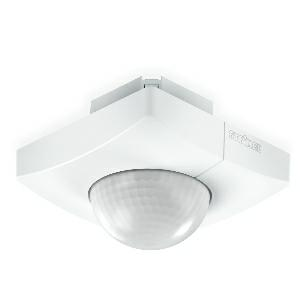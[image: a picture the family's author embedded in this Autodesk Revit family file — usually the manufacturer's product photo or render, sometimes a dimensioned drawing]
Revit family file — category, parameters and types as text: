
# Revit family: is_3360_033491
name_source: partatom
category: Elektroinstallationen
revit_build: Autodesk Revit 2016 (Build: 20190508_0715(x64)
units: mm (PartAtom-declared; Revit-internal decimal feet)

## family parameters
Basisbauteil = Fläche
Beim Laden mit Abzugskörper schneiden = Nein
Bemaßung runder Anschluss = Durchmesser verwenden
Beschriftungsausrichtung beibehalten = Nein
Gemeinsam genutzt = Nein
Raumberechnungspunkt = Nein
Teiletyp = Normal

## types (1)
- IS 3360
    Apparent Load = 0 VA
    Beschreibung = Type: Motion detectors; Dimensions (L x W x H): 78 x 94 x 94 mm; Mains power supply: 220 – 240 V / 50 – 60 Hz; Sensor Technology: passive infrared; Application, place: Indoors; Application, room: production facilities, recreation room, changing room, function room / ancillary room, sports hall, reception / lobby, stairwell, WC / washroom, multi-storey / underground car park, warehouse, Indoors; Installation site: ceiling; Installation: Concealed wiring; Switching zones: 1416 switching zones; Electronic scalability: No; Mechanical scalability: No; Mounting height: 2,50 – 4,00 m; Optimum mounting height: 2,8 m; Detection angle: 360 °; Angle of aperture: 180 °; Sneak-by guard: Yes; Capability of masking out individual segments: Yes; Reach, radial: Ø 8 m (50 m²); Reach, tangential: Ø 40 m (1257 m²); Reach, presence: Ø 3 m (7 m²); Twilight setting TEACH: Yes; Twilight setting: 2 – 1000 lx; Time setting: 5 sec – 15 min; Constant-lighting control: No; Basic light level function: No; Functions: Normal / test mode, Manual ON / ON-OFF; Settings via: Remote control, Potentiometers, Smart Remote; With remote control: No; Interconnection: Yes; IP-rating: IP20; Material: Plastic; Ambient temperature: -20 – 50 °C; Colour: white; Colour, RAL: 9003; Manufacturer's Warranty: 5 years; Version: PF - concealed, sq.; PU1, EAN: 4007841033491
    Height = 0 mm  [stored 0 ft]
    Hersteller = Steinel
    Length = 78 mm  [stored 0.255906 ft]
    Maximum range = 20.158 m
    ModVariant = Nein
    Modell = 033491
    Mounting Place = Ceiling
    Mounting Type = Recessed
    Number of Poles = 1
    OnlyDefault = Ja
    Power Factor = 1
    Product Name = IS 3360
    Product group = Presence detector
    ProductGroupID = 4
    Protection Class = Protection class
    Protection Degree = IP 20
    RlxData = <blob elided: 158749 chars, md5=a83f05b0>
    Sensor characteristics = Circular 300°-360°
    Sensor type = Passive (infrared)
    SensorDataFile = <blob elided: 6785 chars, md5=23016e95>
    Type of entry = Presence, Motion
    Typenbild = produkt1_033491.jpg
    Typenkommentare = Product without accessories
    URL = http://relux.com
    VarID = ---
    Voltage = 0 V
    Vorgabe-Ansicht = 1800 mm
    Weight = 0.00 kg
    Width = 94 mm  [stored 0.308399 ft]

note: [stored X ft] marks values corroborated as IEEE doubles in the binary element streams (Revit-internal decimal feet)

## geometry (parser evidence)
native form markers: Blend x4, Sweep x16
no freeform markers — native parametric forms only
